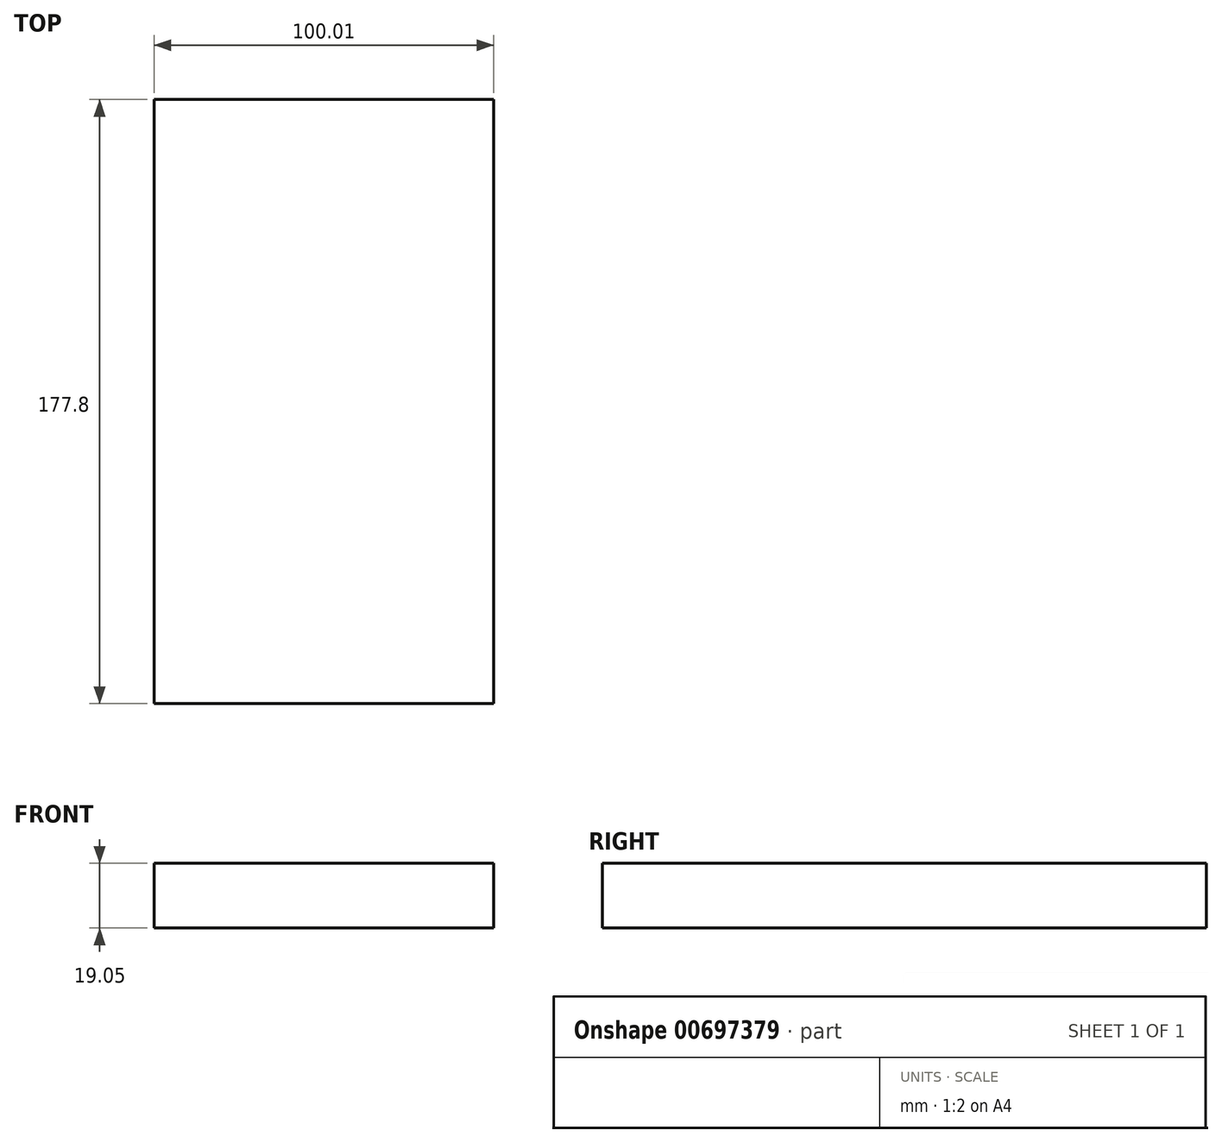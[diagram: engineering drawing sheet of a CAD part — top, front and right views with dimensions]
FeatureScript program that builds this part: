
annotation { "Feature Type Name" : "Feature", "Feature Type Description" : "" }
export const myFeature = defineFeature(function(context is Context, id is Id, definition is map)
    precondition{}
    {
        {
            var Q0;
            Q0=qCreatedBy(makeId("Front.planeOp"),FACE);
            var sketch = newSketch(context, id + "F0", { "sketchPlane" : qUnion([Q0])});
            skLineSegment(sketch, "E0.bottom", {"start": v(0, 0) * mm, "end": v(100.01, 0) * mm});
            skLineSegment(sketch, "E0.top", {"start": v(0, 19.05) * mm, "end": v(100.01, 19.05) * mm});
            skLineSegment(sketch, "E0.left", {"start": v(0, 0) * mm, "end": v(0, 19.05) * mm});
            skLineSegment(sketch, "E0.right", {"start": v(100.01, 0) * mm, "end": v(100.01, 19.05) * mm});
            skSolve(sketch);
        }
        {
            var Q0;
            Q0 = qSketchRegion(id + "F0", true);
            extrude(context, id + "F1", {"entities" : qUnion([Q0]), "oppositeDirection" : true, "depth" : 177.8 * mm, "offsetDistance" : 25.4 * mm});
        }
    });
